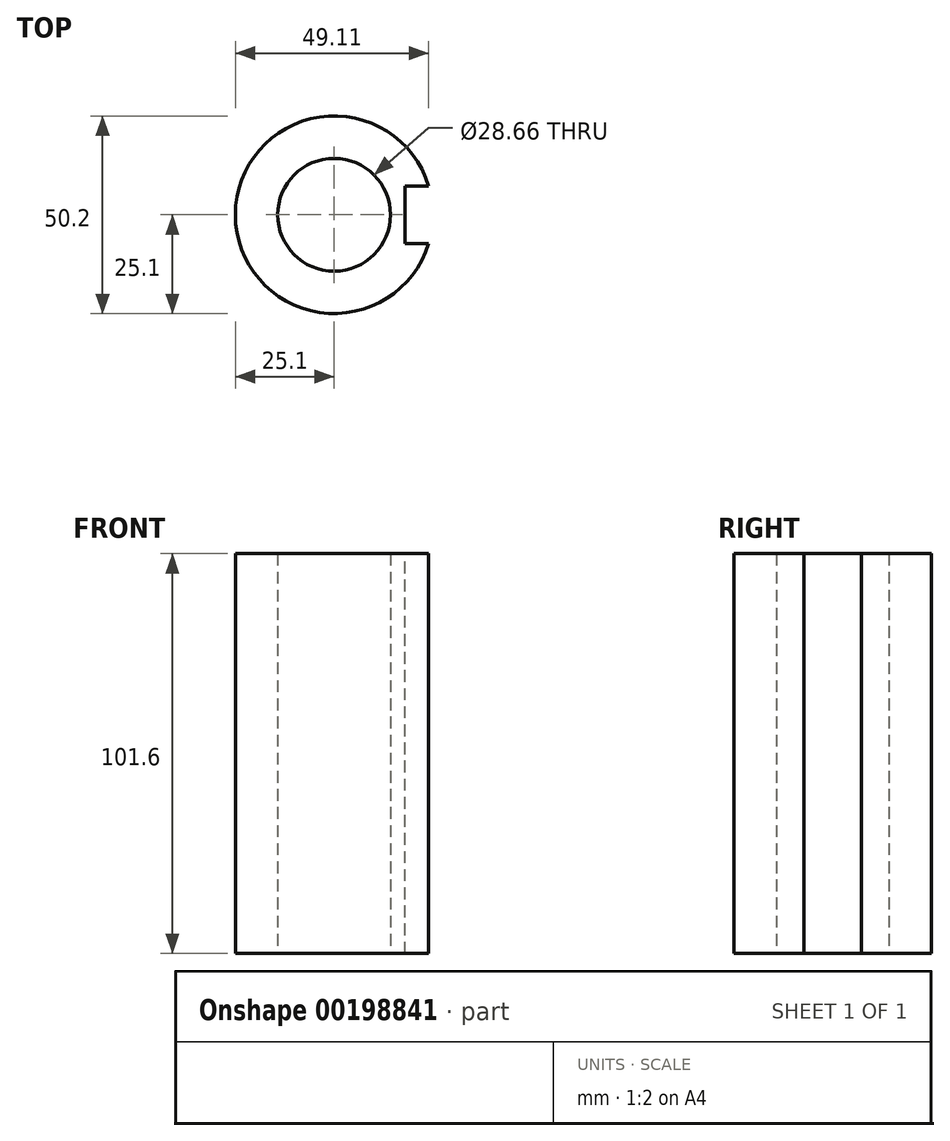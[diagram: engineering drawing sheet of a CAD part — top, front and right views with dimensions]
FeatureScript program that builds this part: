
annotation { "Feature Type Name" : "Feature", "Feature Type Description" : "" }
export const myFeature = defineFeature(function(context is Context, id is Id, definition is map)
    precondition{}
    {
        {
            var Q0;
            Q0=qCreatedBy(makeId("Top.planeOp"),FACE);
            var sketch = newSketch(context, id + "F0", { "sketchPlane" : qUnion([Q0])});
            skCircle(sketch, "E0", {"center": v(0, 0) * mm, "radius": 25.1 * mm});
            skCircle(sketch, "E1", {"center": v(0, 0) * mm, "radius": 14.33 * mm});
            skSolve(sketch);
        }
        {
            var Q0;
            Q0=makeQuery(id+"F0.imprint","IMPRINT",FACE,{"disambiguationData":[TD([[makeQuery(id+"F0.imprint","IMPRINT",EDGE,{"derivedFrom":sQuery(id+"F0.wireOp",EDGE,"E0")}),1.0]])]});
            extrude(context, id + "F1", {"entities" : qUnion([Q0]), "endBound" : BoundingType.SYMMETRIC, "depth" : 101.6 * mm});
        }
        {
            var Q0;
            Q0=qCreatedBy(makeId("Top.planeOp"),FACE);
            var sketch = newSketch(context, id + "F2", { "sketchPlane" : qUnion([Q0])});
            skLineSegment(sketch, "E2.bottom", {"start": v(18.02, -7.31) * mm, "end": v(32.98, -7.31) * mm});
            skLineSegment(sketch, "E2.top", {"start": v(18.02, 7.31) * mm, "end": v(32.98, 7.31) * mm});
            skLineSegment(sketch, "E2.left", {"start": v(18.02, -7.31) * mm, "end": v(18.02, 7.31) * mm});
            skLineSegment(sketch, "E2.right", {"start": v(32.98, -7.31) * mm, "end": v(32.98, 7.31) * mm});
            skPoint(sketch, "E2.middle", {"position": v(25.5, 0) * mm});
            skSolve(sketch);
        }
        {
            var Q0;
            Q0 = qSketchRegion(id + "F2", true);
            extrude(context, id + "F3", {"entities" : qUnion([Q0]), "operationType" : NewBodyOperationType.REMOVE, "endBound" : BoundingType.SYMMETRIC, "oppositeDirection" : true, "depth" : 101.6 * mm});
        }
    });
